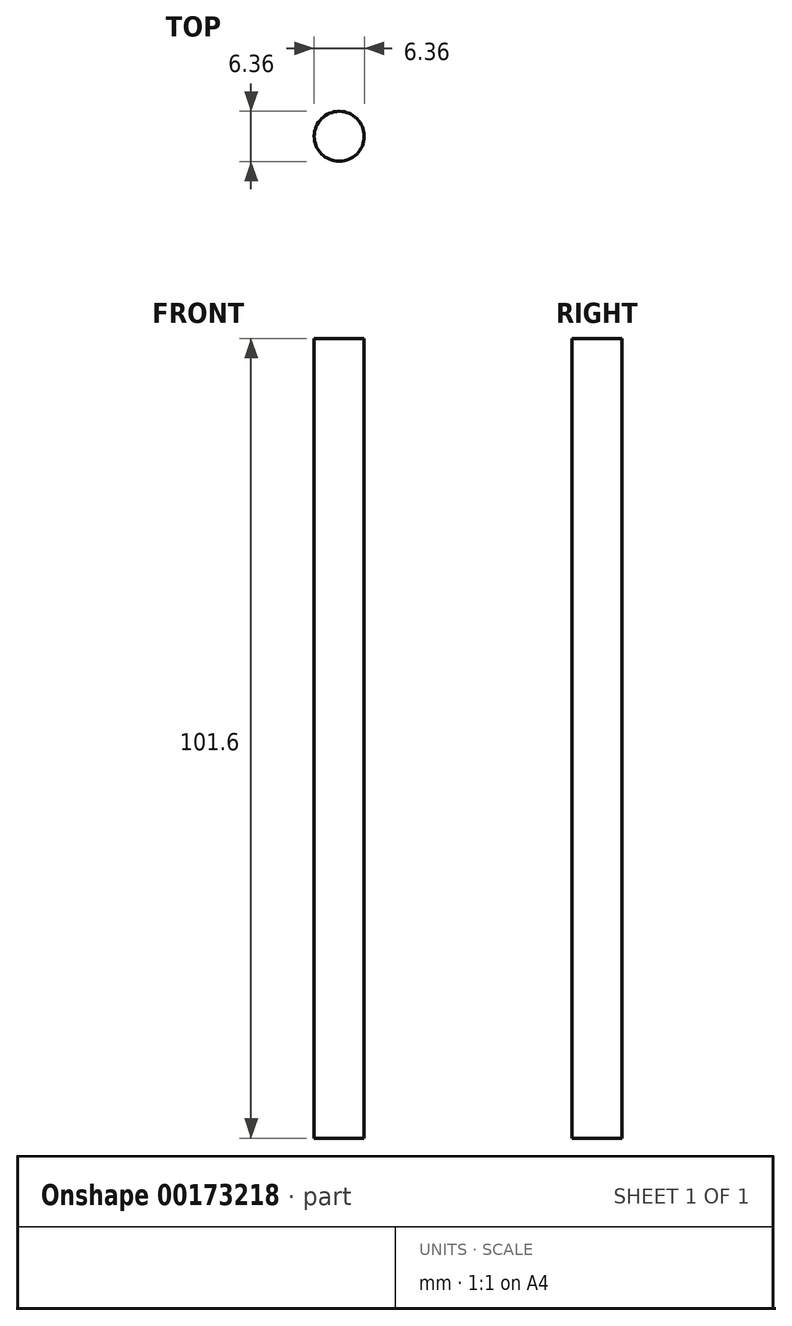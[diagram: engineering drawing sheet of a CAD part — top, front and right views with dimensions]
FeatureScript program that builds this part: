
annotation { "Feature Type Name" : "Feature", "Feature Type Description" : "" }
export const myFeature = defineFeature(function(context is Context, id is Id, definition is map)
    precondition{}
    {
        {
            var Q0;
            Q0=qCreatedBy(makeId("Top.planeOp"),FACE);
            var sketch = newSketch(context, id + "F0", { "sketchPlane" : qUnion([Q0])});
            skCircle(sketch, "E0", {"center": v(0, 0) * mm, "radius": 3.18 * mm});
            skSolve(sketch);
        }
        {
            var Q0;
            Q0=makeQuery(id+"F0.imprint","IMPRINT",FACE,{"disambiguationData":[TD([[makeQuery(id+"F0.imprint","IMPRINT",EDGE,{"derivedFrom":sQuery(id+"F0.wireOp",EDGE,"E0")}),1.0]])]});
            extrude(context, id + "F1", {"entities" : qUnion([Q0]), "depth" : 101.6 * mm});
        }
    });
